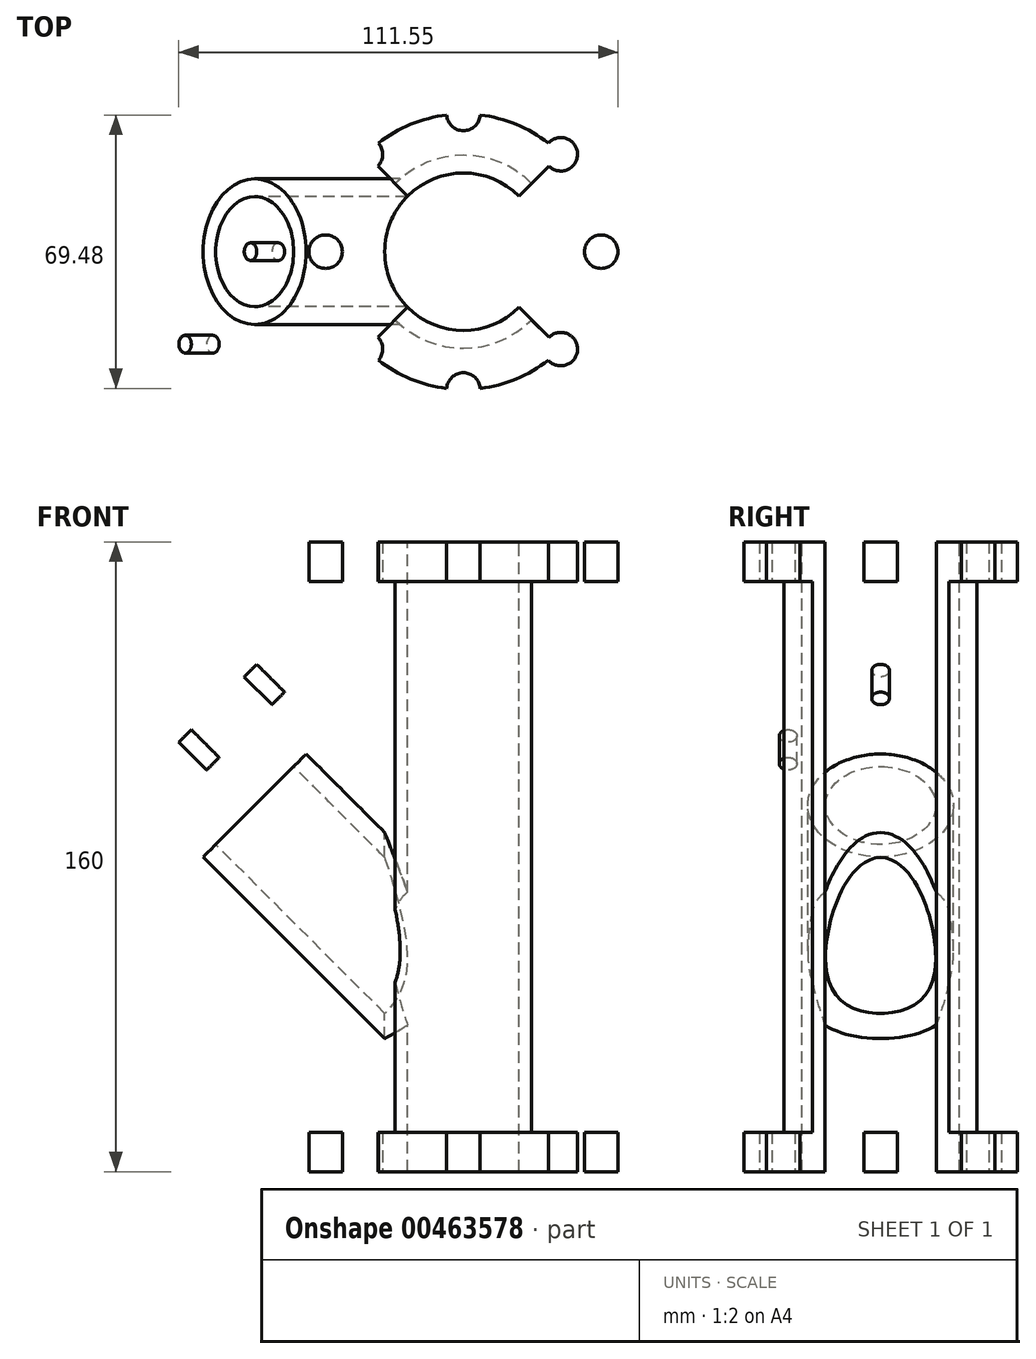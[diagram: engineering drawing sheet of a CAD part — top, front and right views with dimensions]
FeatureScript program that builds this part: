
annotation { "Feature Type Name" : "Feature", "Feature Type Description" : "" }
export const myFeature = defineFeature(function(context is Context, id is Id, definition is map)
    precondition{}
    {
        {
            var Q0;
            Q0=qCreatedBy(makeId("Top.planeOp"),FACE);
            var sketch = newSketch(context, id + "F0", { "sketchPlane" : qUnion([Q0])});
            skCircle(sketch, "E0", {"center": v(0, 0) * mm, "radius": 45 * mm});
            skSolve(sketch);
        }
        {
            var Q0;
            Q0 = qSketchRegion(id + "F0", true);
            extrude(context, id + "F1", {"entities" : qUnion([Q0]), "depth" : 10 * mm});
        }
        {
            var Q0;
            Q0=makeQuery(id+"F1.opExtrude","CAP_FACE",FACE,{"disambiguationData":[OSD([sQuery(id+"F0.wireOp",EDGE,"E0")])],"isStart":false});
            var sketch = newSketch(context, id + "F2", { "sketchPlane" : qUnion([Q0])});
            skCircle(sketch, "E1", {"center": v(0, 0) * mm, "radius": 24.5 * mm});
            skCircle(sketch, "E2", {"center": v(0, 0) * mm, "radius": 20 * mm});
            skSolve(sketch);
        }
        {
            var Q0;
            Q0 = qSketchRegion(id + "F2", true);
            var Q1;
            Q1=makeQuery(id+"F2.imprint","IMPRINT",FACE,{"disambiguationData":[TD([[makeQuery(id+"F2.imprint","IMPRINT",EDGE,{"derivedFrom":sQuery(id+"F2.wireOp",EDGE,"E2")}),1.0]])]});
            extrude(context, id + "F3", {"entities" : qUnion([Q0, Q1]), "operationType" : NewBodyOperationType.ADD, "depth" : 140 * mm});
        }
        {
            var Q0;
            Q0=makeQuery(id+"F3.opExtrude","CAP_FACE",FACE,{"disambiguationData":[OSD([sQuery(id+"F2.wireOp",EDGE,"E1")])],"isStart":false});
            var sketch = newSketch(context, id + "F4", { "sketchPlane" : qUnion([Q0])});
            skCircle(sketch, "E3", {"center": v(0, 0) * mm, "radius": 45 * mm});
            skCircle(sketch, "E4", {"center": v(0, 0) * mm, "radius": 24.5 * mm});
            skCircle(sketch, "E5", {"center": v(0, 0) * mm, "radius": 20 * mm});
            skSolve(sketch);
        }
        {
            var Q0;
            Q0 = qSketchRegion(id + "F4", true);
            var Q1;
            Q1=makeQuery(id+"F4.imprint","IMPRINT",FACE,{"disambiguationData":[TD([[makeQuery(id+"F4.imprint","IMPRINT",EDGE,{"derivedFrom":sQuery(id+"F4.wireOp",EDGE,"E5")}),1.0]])]});
            var Q2;
            Q2=makeQuery(id+"F4.imprint","IMPRINT",FACE,{"disambiguationData":[TD([[makeQuery(id+"F4.imprint","IMPRINT",EDGE,{"derivedFrom":sQuery(id+"F4.wireOp",EDGE,"E4")}),1.0]])]});
            extrude(context, id + "F5", {"entities" : qUnion([Q0, Q1, Q2]), "operationType" : NewBodyOperationType.ADD, "depth" : 10 * mm});
        }
        {
            var Q0;
            Q0=makeQuery(id+"F5.opExtrude","CAP_FACE",FACE,{"disambiguationData":[OSD([sQuery(id+"F4.wireOp",EDGE,"E3")])],"isStart":false});
            var sketch = newSketch(context, id + "F6", { "sketchPlane" : qUnion([Q0])});
            skSolve(sketch);
        }
        {
            var Q0;
            Q0=makeQuery(id+"F1.opExtrude","CAP_FACE",FACE,{"disambiguationData":[OSD([sQuery(id+"F0.wireOp",EDGE,"E0")])],"isStart":true});
            var sketch = newSketch(context, id + "F7", { "sketchPlane" : qUnion([Q0])});
            skCircle(sketch, "E6", {"center": v(0, 0) * mm, "radius": 35 * mm});
            skCircle(sketch, "E7", {"center": v(0, 35) * mm, "radius": 4.25 * mm});
            skCircle(sketch, "E8", {"center": v(35, 0) * mm, "radius": 4.25 * mm});
            skCircle(sketch, "E9", {"center": v(0, -35) * mm, "radius": 4.25 * mm});
            skCircle(sketch, "E10", {"center": v(-35, 0) * mm, "radius": 4.25 * mm});
            skLineSegment(sketch, "E11", {"start": v(0, 0) * mm, "end": v(7, 0) * mm});
            skLineSegment(sketch, "E12", {"start": v(0, 0) * mm, "end": v(0, -7) * mm});
            skLineSegment(sketch, "E13", {"start": v(0, 0) * mm, "end": v(-7, 0) * mm});
            skLineSegment(sketch, "E14", {"start": v(0, 0) * mm, "end": v(0, 7) * mm});
            skLineSegment(sketch, "E15", {"start": v(7, 0) * mm, "end": v(7, 7) * mm});
            skLineSegment(sketch, "E16", {"start": v(7, 7) * mm, "end": v(0, 7) * mm});
            skLineSegment(sketch, "E17", {"start": v(0, 7) * mm, "end": v(-7, 7) * mm});
            skLineSegment(sketch, "E18", {"start": v(-7, 7) * mm, "end": v(-7, 0) * mm});
            skLineSegment(sketch, "E19", {"start": v(-7, -7) * mm, "end": v(0, -7) * mm});
            skLineSegment(sketch, "E20", {"start": v(-7, -7) * mm, "end": v(-7, 0) * mm});
            skLineSegment(sketch, "E21", {"start": v(0, -7) * mm, "end": v(7, -7) * mm});
            skLineSegment(sketch, "E22", {"start": v(7, -7) * mm, "end": v(7, 0) * mm});
            skLineSegment(sketch, "E23", {"start": v(-7, -7) * mm, "end": v(7, 7) * mm});
            skLineSegment(sketch, "E24", {"start": v(7, -7) * mm, "end": v(-7, 7) * mm});
            skLineSegment(sketch, "E25", {"start": v(7, 7) * mm, "end": v(24.75, 24.75) * mm});
            skLineSegment(sketch, "E26", {"start": v(24.75, 24.75) * mm, "end": v(-24.75, -24.75) * mm});
            skLineSegment(sketch, "E27", {"start": v(-7, 7) * mm, "end": v(24.75, -24.75) * mm});
            skLineSegment(sketch, "E28", {"start": v(24.75, -24.75) * mm, "end": v(-24.75, 24.75) * mm});
            skCircle(sketch, "E29", {"center": v(-24.75, 24.75) * mm, "radius": 4.25 * mm});
            skCircle(sketch, "E30", {"center": v(24.75, 24.75) * mm, "radius": 4.25 * mm});
            skCircle(sketch, "E31", {"center": v(24.75, -24.75) * mm, "radius": 4.25 * mm});
            skCircle(sketch, "E32", {"center": v(-24.75, -24.75) * mm, "radius": 4.25 * mm});
            skSolve(sketch);
        }
        {
            var Q0;
            {var subQ0=sQuery(id+"F7.wireOp",EDGE,"E10");var subQ1=sQuery(id+"F7.wireOp",EDGE,"E6");var subQ2=makeQuery(id+"F7.imprint","INTERSECT",VERTEX,{"disambiguationData":[OD(0.0)],"derivedFrom":[subQ1,subQ0]});Q0=makeQuery(id+"F7.imprint","IMPRINT",FACE,{"disambiguationData":[TD([[makeQuery(id+"F7.imprint","IMPRINT",EDGE,{"disambiguationData":[TD([[subQ2,-1.0]])],"derivedFrom":subQ1}),-1.0]])]});}
            var Q1;
            {var subQ0=sQuery(id+"F7.wireOp",EDGE,"E10");var subQ1=sQuery(id+"F7.wireOp",EDGE,"E6");var subQ2=makeQuery(id+"F7.imprint","INTERSECT",VERTEX,{"disambiguationData":[OD(0.0)],"derivedFrom":[subQ1,subQ0]});Q1=makeQuery(id+"F7.imprint","IMPRINT",FACE,{"disambiguationData":[TD([[makeQuery(id+"F7.imprint","IMPRINT",EDGE,{"disambiguationData":[TD([[subQ2,-1.0]])],"derivedFrom":subQ1}),1.0]])]});}
            var Q2;
            {var subQ0=sQuery(id+"F7.wireOp",EDGE,"E9");var subQ1=sQuery(id+"F7.wireOp",EDGE,"E6");var subQ2=makeQuery(id+"F7.imprint","INTERSECT",VERTEX,{"disambiguationData":[OD(0.0)],"derivedFrom":[subQ1,subQ0]});Q2=makeQuery(id+"F7.imprint","IMPRINT",FACE,{"disambiguationData":[TD([[makeQuery(id+"F7.imprint","IMPRINT",EDGE,{"disambiguationData":[TD([[subQ2,-1.0]])],"derivedFrom":subQ1}),1.0]])]});}
            var Q3;
            {var subQ0=sQuery(id+"F7.wireOp",EDGE,"E9");var subQ1=sQuery(id+"F7.wireOp",EDGE,"E6");var subQ2=makeQuery(id+"F7.imprint","INTERSECT",VERTEX,{"disambiguationData":[OD(0.0)],"derivedFrom":[subQ1,subQ0]});Q3=makeQuery(id+"F7.imprint","IMPRINT",FACE,{"disambiguationData":[TD([[makeQuery(id+"F7.imprint","IMPRINT",EDGE,{"disambiguationData":[TD([[subQ2,-1.0]])],"derivedFrom":subQ1}),-1.0]])]});}
            var Q4;
            {var subQ0=sQuery(id+"F7.wireOp",EDGE,"E8");var subQ1=sQuery(id+"F7.wireOp",EDGE,"E6");var subQ2=makeQuery(id+"F7.imprint","INTERSECT",VERTEX,{"disambiguationData":[OD(0.0)],"derivedFrom":[subQ1,subQ0]});Q4=makeQuery(id+"F7.imprint","IMPRINT",FACE,{"disambiguationData":[TD([[makeQuery(id+"F7.imprint","IMPRINT",EDGE,{"disambiguationData":[TD([[subQ2,1.0]])],"derivedFrom":subQ1}),1.0]])]});}
            var Q5;
            {var subQ0=sQuery(id+"F7.wireOp",EDGE,"E8");var subQ1=sQuery(id+"F7.wireOp",EDGE,"E6");var subQ2=makeQuery(id+"F7.imprint","INTERSECT",VERTEX,{"disambiguationData":[OD(0.0)],"derivedFrom":[subQ1,subQ0]});Q5=makeQuery(id+"F7.imprint","IMPRINT",FACE,{"disambiguationData":[TD([[makeQuery(id+"F7.imprint","IMPRINT",EDGE,{"disambiguationData":[TD([[subQ2,1.0]])],"derivedFrom":subQ1}),-1.0]])]});}
            var Q6;
            {var subQ0=sQuery(id+"F7.wireOp",EDGE,"E6");var subQ1=makeQuery(id+"F7.imprint","INTERSECT",VERTEX,{"disambiguationData":[OD(0.0)],"derivedFrom":[subQ0,sQuery(id+"F7.wireOp",EDGE,"E26")]});Q6=makeQuery(id+"F7.imprint","IMPRINT",FACE,{"disambiguationData":[TD([[makeQuery(id+"F7.imprint","IMPRINT",EDGE,{"disambiguationData":[TD([[subQ1,1.0]])],"derivedFrom":subQ0}),-1.0]])]});}
            var Q7;
            {var subQ0=sQuery(id+"F7.wireOp",EDGE,"E26");var subQ1=sQuery(id+"F7.wireOp",EDGE,"E6");var subQ2=makeQuery(id+"F7.imprint","INTERSECT",VERTEX,{"disambiguationData":[OD(0.0)],"derivedFrom":[subQ1,subQ0]});Q7=makeQuery(id+"F7.imprint","IMPRINT",FACE,{"disambiguationData":[TD([[makeQuery(id+"F7.imprint","IMPRINT",EDGE,{"disambiguationData":[TD([[subQ2,1.0]])],"derivedFrom":subQ1}),1.0]])]});}
            var Q8;
            {var subQ0=sQuery(id+"F7.wireOp",EDGE,"E26");var subQ1=sQuery(id+"F7.wireOp",EDGE,"E6");var subQ2=makeQuery(id+"F7.imprint","INTERSECT",VERTEX,{"disambiguationData":[OD(0.0)],"derivedFrom":[subQ1,subQ0]});Q8=makeQuery(id+"F7.imprint","IMPRINT",FACE,{"disambiguationData":[TD([[makeQuery(id+"F7.imprint","IMPRINT",EDGE,{"disambiguationData":[TD([[subQ2,-1.0]])],"derivedFrom":subQ1}),1.0]])]});}
            var Q9;
            {var subQ0=sQuery(id+"F7.wireOp",EDGE,"E6");var subQ1=makeQuery(id+"F7.imprint","INTERSECT",VERTEX,{"disambiguationData":[OD(1.0)],"derivedFrom":[subQ0,sQuery(id+"F7.wireOp",EDGE,"E28")]});Q9=makeQuery(id+"F7.imprint","IMPRINT",FACE,{"disambiguationData":[TD([[makeQuery(id+"F7.imprint","IMPRINT",EDGE,{"disambiguationData":[TD([[subQ1,1.0]])],"derivedFrom":subQ0}),-1.0]])]});}
            var Q10;
            {var subQ0=sQuery(id+"F7.wireOp",EDGE,"E28");var subQ1=sQuery(id+"F7.wireOp",EDGE,"E6");var subQ2=makeQuery(id+"F7.imprint","INTERSECT",VERTEX,{"disambiguationData":[OD(1.0)],"derivedFrom":[subQ1,subQ0]});Q10=makeQuery(id+"F7.imprint","IMPRINT",FACE,{"disambiguationData":[TD([[makeQuery(id+"F7.imprint","IMPRINT",EDGE,{"disambiguationData":[TD([[subQ2,1.0]])],"derivedFrom":subQ1}),1.0]])]});}
            var Q11;
            {var subQ0=sQuery(id+"F7.wireOp",EDGE,"E28");var subQ1=sQuery(id+"F7.wireOp",EDGE,"E6");var subQ2=makeQuery(id+"F7.imprint","INTERSECT",VERTEX,{"disambiguationData":[OD(1.0)],"derivedFrom":[subQ1,subQ0]});Q11=makeQuery(id+"F7.imprint","IMPRINT",FACE,{"disambiguationData":[TD([[makeQuery(id+"F7.imprint","IMPRINT",EDGE,{"disambiguationData":[TD([[subQ2,-1.0]])],"derivedFrom":subQ1}),1.0]])]});}
            var Q12;
            {var subQ0=sQuery(id+"F7.wireOp",EDGE,"E6");var subQ1=makeQuery(id+"F7.imprint","INTERSECT",VERTEX,{"disambiguationData":[OD(1.0)],"derivedFrom":[subQ0,sQuery(id+"F7.wireOp",EDGE,"E26")]});Q12=makeQuery(id+"F7.imprint","IMPRINT",FACE,{"disambiguationData":[TD([[makeQuery(id+"F7.imprint","IMPRINT",EDGE,{"disambiguationData":[TD([[subQ1,1.0]])],"derivedFrom":subQ0}),-1.0]])]});}
            var Q13;
            {var subQ0=sQuery(id+"F7.wireOp",EDGE,"E26");var subQ1=sQuery(id+"F7.wireOp",EDGE,"E6");var subQ2=makeQuery(id+"F7.imprint","INTERSECT",VERTEX,{"disambiguationData":[OD(1.0)],"derivedFrom":[subQ1,subQ0]});Q13=makeQuery(id+"F7.imprint","IMPRINT",FACE,{"disambiguationData":[TD([[makeQuery(id+"F7.imprint","IMPRINT",EDGE,{"disambiguationData":[TD([[subQ2,1.0]])],"derivedFrom":subQ1}),1.0]])]});}
            var Q14;
            {var subQ0=sQuery(id+"F7.wireOp",EDGE,"E26");var subQ1=sQuery(id+"F7.wireOp",EDGE,"E6");var subQ2=makeQuery(id+"F7.imprint","INTERSECT",VERTEX,{"disambiguationData":[OD(1.0)],"derivedFrom":[subQ1,subQ0]});Q14=makeQuery(id+"F7.imprint","IMPRINT",FACE,{"disambiguationData":[TD([[makeQuery(id+"F7.imprint","IMPRINT",EDGE,{"disambiguationData":[TD([[subQ2,-1.0]])],"derivedFrom":subQ1}),1.0]])]});}
            var Q15;
            {var subQ0=sQuery(id+"F7.wireOp",EDGE,"E6");var subQ1=makeQuery(id+"F7.imprint","INTERSECT",VERTEX,{"disambiguationData":[OD(0.0)],"derivedFrom":[subQ0,sQuery(id+"F7.wireOp",EDGE,"E28")]});Q15=makeQuery(id+"F7.imprint","IMPRINT",FACE,{"disambiguationData":[TD([[makeQuery(id+"F7.imprint","IMPRINT",EDGE,{"disambiguationData":[TD([[subQ1,1.0]])],"derivedFrom":subQ0}),-1.0]])]});}
            var Q16;
            {var subQ0=sQuery(id+"F7.wireOp",EDGE,"E28");var subQ1=sQuery(id+"F7.wireOp",EDGE,"E6");var subQ2=makeQuery(id+"F7.imprint","INTERSECT",VERTEX,{"disambiguationData":[OD(0.0)],"derivedFrom":[subQ1,subQ0]});Q16=makeQuery(id+"F7.imprint","IMPRINT",FACE,{"disambiguationData":[TD([[makeQuery(id+"F7.imprint","IMPRINT",EDGE,{"disambiguationData":[TD([[subQ2,1.0]])],"derivedFrom":subQ1}),1.0]])]});}
            var Q17;
            {var subQ0=sQuery(id+"F7.wireOp",EDGE,"E28");var subQ1=sQuery(id+"F7.wireOp",EDGE,"E6");var subQ2=makeQuery(id+"F7.imprint","INTERSECT",VERTEX,{"disambiguationData":[OD(0.0)],"derivedFrom":[subQ1,subQ0]});Q17=makeQuery(id+"F7.imprint","IMPRINT",FACE,{"disambiguationData":[TD([[makeQuery(id+"F7.imprint","IMPRINT",EDGE,{"disambiguationData":[TD([[subQ2,-1.0]])],"derivedFrom":subQ1}),1.0]])]});}
            var Q18;
            {var subQ0=sQuery(id+"F7.wireOp",EDGE,"E7");var subQ1=sQuery(id+"F7.wireOp",EDGE,"E6");var subQ2=makeQuery(id+"F7.imprint","INTERSECT",VERTEX,{"disambiguationData":[OD(0.0)],"derivedFrom":[subQ1,subQ0]});Q18=makeQuery(id+"F7.imprint","IMPRINT",FACE,{"disambiguationData":[TD([[makeQuery(id+"F7.imprint","IMPRINT",EDGE,{"disambiguationData":[TD([[subQ2,-1.0]])],"derivedFrom":subQ1}),1.0]])]});}
            var Q19;
            {var subQ0=sQuery(id+"F7.wireOp",EDGE,"E7");var subQ1=sQuery(id+"F7.wireOp",EDGE,"E6");var subQ2=makeQuery(id+"F7.imprint","INTERSECT",VERTEX,{"disambiguationData":[OD(0.0)],"derivedFrom":[subQ1,subQ0]});Q19=makeQuery(id+"F7.imprint","IMPRINT",FACE,{"disambiguationData":[TD([[makeQuery(id+"F7.imprint","IMPRINT",EDGE,{"disambiguationData":[TD([[subQ2,-1.0]])],"derivedFrom":subQ1}),-1.0]])]});}
            extrude(context, id + "F8", {"entities" : qUnion([Q0, Q1, Q2, Q3, Q4, Q5, Q6, Q7, Q8, Q9, Q10, Q11, Q12, Q13, Q14, Q15, Q16, Q17, Q18, Q19]), "operationType" : NewBodyOperationType.REMOVE, "oppositeDirection" : true, "depth" : 195 * mm});
        }
        {
            var Q0;
            Q0=qCreatedBy(makeId("Front.planeOp"),FACE);
            var sketch = newSketch(context, id + "F9", { "sketchPlane" : qUnion([Q0])});
            skLineSegment(sketch, "E33", {"start": v(0, 0) * mm, "end": v(0, 40) * mm});
            skLineSegment(sketch, "E34", {"start": v(0, 40) * mm, "end": v(0, 93.3) * mm});
            skLineSegment(sketch, "E35", {"start": v(0, 40) * mm, "end": v(-63.64, 103.64) * mm});
            skLineSegment(sketch, "E36", {"start": v(-63.64, 103.64) * mm, "end": v(-50.56, 116.72) * mm});
            skLineSegment(sketch, "E37", {"start": v(-50.56, 116.72) * mm, "end": v(-76.72, 90.56) * mm});
            skLineSegment(sketch, "E38", {"start": v(-76.72, 90.56) * mm, "end": v(0, 13.84) * mm});
            skLineSegment(sketch, "E39", {"start": v(0, 13.84) * mm, "end": v(0, 40) * mm});
            skLineSegment(sketch, "E40", {"start": v(-50.56, 116.72) * mm, "end": v(6.24, 59.92) * mm});
            skLineSegment(sketch, "E41", {"start": v(6.24, 59.92) * mm, "end": v(0, 13.84) * mm});
            skSolve(sketch);
        }
        {
            var Q0;
            Q0 = qSketchRegion(id + "F9", true);
            extrude(context, id + "F10", {"entities" : qUnion([Q0]), "operationType" : NewBodyOperationType.ADD, "endBound" : BoundingType.SYMMETRIC, "depth" : 37 * mm});
        }
        {
            var Q0;
            Q0=makeQuery(id+"F10.opExtrude","CAP_EDGE",EDGE,{"disambiguationData":[OSD([sQuery(id+"F9.wireOp",EDGE,"E38")])],"isStart":true});
            var Q1;
            Q1=makeQuery(id+"F10.opExtrude","CAP_EDGE",EDGE,{"disambiguationData":[OSD([sQuery(id+"F9.wireOp",EDGE,"E38")])],"isStart":false});
            var Q2;
            Q2=makeQuery(id+"F10.opExtrude","CAP_EDGE",EDGE,{"disambiguationData":[OSD([sQuery(id+"F9.wireOp",EDGE,"E40")])],"isStart":false});
            var Q3;
            Q3=makeQuery(id+"F10.opExtrude","CAP_EDGE",EDGE,{"disambiguationData":[OSD([sQuery(id+"F9.wireOp",EDGE,"E40")])],"isStart":true});
            fillet(context, id + "F11", {"entities" : qUnion([Q0, Q1, Q2, Q3]), "radius" : 18.5 * mm, "tangentPropagation" : true, "allowEdgeOverflow" : false});
        }
        {
            var Q0;
            Q0=makeQuery(id+"F10.opExtrude","SWEPT_FACE",FACE,{"disambiguationData":[OSD([sQuery(id+"F9.wireOp",EDGE,"E37")])]});
            var sketch = newSketch(context, id + "F12", { "sketchPlane" : qUnion([Q0])});
            skCircle(sketch, "E42", {"center": v(0, 28.28) * mm, "radius": 28.5 * mm});
            skSolve(sketch);
        }
        {
            var Q0;
            Q0 = qSketchRegion(id + "F12", true);
            extrude(context, id + "F13", {"entities" : qUnion([Q0]), "operationType" : NewBodyOperationType.ADD, "depth" : 10 * mm});
        }
        {
            var Q0;
            Q0=makeQuery(id+"F13.opExtrude","CAP_FACE",FACE,{"disambiguationData":[OSD([sQuery(id+"F12.wireOp",EDGE,"E42")])],"isStart":false});
            var sketch = newSketch(context, id + "F14", { "sketchPlane" : qUnion([Q0])});
            skCircle(sketch, "E43", {"center": v(0, 28.28) * mm, "radius": 23.5 * mm});
            skCircle(sketch, "E44", {"center": v(0, 51.78) * mm, "radius": 2.25 * mm});
            skCircle(sketch, "E45", {"center": v(23.5, 28.28) * mm, "radius": 2.25 * mm});
            skCircle(sketch, "E46", {"center": v(-23.5, 28.28) * mm, "radius": 2.25 * mm});
            skCircle(sketch, "E47", {"center": v(0, 4.78) * mm, "radius": 2.25 * mm});
            skSolve(sketch);
        }
        {
            var Q0;
            {var subQ0=sQuery(id+"F14.wireOp",EDGE,"E44");var subQ1=sQuery(id+"F14.wireOp",EDGE,"E43");var subQ2=makeQuery(id+"F14.imprint","INTERSECT",VERTEX,{"disambiguationData":[OD(0.0)],"derivedFrom":[subQ1,subQ0]});Q0=makeQuery(id+"F14.imprint","IMPRINT",FACE,{"disambiguationData":[TD([[makeQuery(id+"F14.imprint","IMPRINT",EDGE,{"disambiguationData":[TD([[subQ2,-1.0]])],"derivedFrom":subQ1}),1.0]])]});}
            var Q1;
            {var subQ0=sQuery(id+"F14.wireOp",EDGE,"E44");var subQ1=sQuery(id+"F14.wireOp",EDGE,"E43");var subQ2=makeQuery(id+"F14.imprint","INTERSECT",VERTEX,{"disambiguationData":[OD(0.0)],"derivedFrom":[subQ1,subQ0]});Q1=makeQuery(id+"F14.imprint","IMPRINT",FACE,{"disambiguationData":[TD([[makeQuery(id+"F14.imprint","IMPRINT",EDGE,{"disambiguationData":[TD([[subQ2,-1.0]])],"derivedFrom":subQ1}),-1.0]])]});}
            var Q2;
            {var subQ0=sQuery(id+"F14.wireOp",EDGE,"E46");var subQ1=sQuery(id+"F14.wireOp",EDGE,"E43");var subQ2=makeQuery(id+"F14.imprint","INTERSECT",VERTEX,{"disambiguationData":[OD(0.0)],"derivedFrom":[subQ1,subQ0]});Q2=makeQuery(id+"F14.imprint","IMPRINT",FACE,{"disambiguationData":[TD([[makeQuery(id+"F14.imprint","IMPRINT",EDGE,{"disambiguationData":[TD([[subQ2,-1.0]])],"derivedFrom":subQ1}),-1.0]])]});}
            var Q3;
            {var subQ0=sQuery(id+"F14.wireOp",EDGE,"E46");var subQ1=sQuery(id+"F14.wireOp",EDGE,"E43");var subQ2=makeQuery(id+"F14.imprint","INTERSECT",VERTEX,{"disambiguationData":[OD(0.0)],"derivedFrom":[subQ1,subQ0]});Q3=makeQuery(id+"F14.imprint","IMPRINT",FACE,{"disambiguationData":[TD([[makeQuery(id+"F14.imprint","IMPRINT",EDGE,{"disambiguationData":[TD([[subQ2,-1.0]])],"derivedFrom":subQ1}),1.0]])]});}
            var Q4;
            {var subQ0=sQuery(id+"F14.wireOp",EDGE,"E47");var subQ1=sQuery(id+"F14.wireOp",EDGE,"E43");var subQ2=makeQuery(id+"F14.imprint","INTERSECT",VERTEX,{"disambiguationData":[OD(0.0)],"derivedFrom":[subQ1,subQ0]});Q4=makeQuery(id+"F14.imprint","IMPRINT",FACE,{"disambiguationData":[TD([[makeQuery(id+"F14.imprint","IMPRINT",EDGE,{"disambiguationData":[TD([[subQ2,-1.0]])],"derivedFrom":subQ1}),1.0]])]});}
            var Q5;
            {var subQ0=sQuery(id+"F14.wireOp",EDGE,"E47");var subQ1=sQuery(id+"F14.wireOp",EDGE,"E43");var subQ2=makeQuery(id+"F14.imprint","INTERSECT",VERTEX,{"disambiguationData":[OD(0.0)],"derivedFrom":[subQ1,subQ0]});Q5=makeQuery(id+"F14.imprint","IMPRINT",FACE,{"disambiguationData":[TD([[makeQuery(id+"F14.imprint","IMPRINT",EDGE,{"disambiguationData":[TD([[subQ2,-1.0]])],"derivedFrom":subQ1}),-1.0]])]});}
            var Q6;
            {var subQ0=sQuery(id+"F14.wireOp",EDGE,"E45");var subQ1=sQuery(id+"F14.wireOp",EDGE,"E43");var subQ2=makeQuery(id+"F14.imprint","INTERSECT",VERTEX,{"disambiguationData":[OD(0.0)],"derivedFrom":[subQ1,subQ0]});Q6=makeQuery(id+"F14.imprint","IMPRINT",FACE,{"disambiguationData":[TD([[makeQuery(id+"F14.imprint","IMPRINT",EDGE,{"disambiguationData":[TD([[subQ2,1.0]])],"derivedFrom":subQ1}),1.0]])]});}
            var Q7;
            {var subQ0=sQuery(id+"F14.wireOp",EDGE,"E45");var subQ1=sQuery(id+"F14.wireOp",EDGE,"E43");var subQ2=makeQuery(id+"F14.imprint","INTERSECT",VERTEX,{"disambiguationData":[OD(0.0)],"derivedFrom":[subQ1,subQ0]});Q7=makeQuery(id+"F14.imprint","IMPRINT",FACE,{"disambiguationData":[TD([[makeQuery(id+"F14.imprint","IMPRINT",EDGE,{"disambiguationData":[TD([[subQ2,1.0]])],"derivedFrom":subQ1}),-1.0]])]});}
            extrude(context, id + "F15", {"entities" : qUnion([Q0, Q1, Q2, Q3, Q4, Q5, Q6, Q7]), "operationType" : NewBodyOperationType.REMOVE, "oppositeDirection" : true, "depth" : 25 * mm});
        }
        {
            var Q0;
            Q0=makeQuery(id+"F13.opExtrude","CAP_FACE",FACE,{"disambiguationData":[OSD([sQuery(id+"F12.wireOp",EDGE,"E42")])],"isStart":false});
            var sketch = newSketch(context, id + "F16", { "sketchPlane" : qUnion([Q0])});
            skCircle(sketch, "E48", {"center": v(0, 28.28) * mm, "radius": 14 * mm});
            skSolve(sketch);
        }
        {
            var Q0;
            Q0 = qSketchRegion(id + "F16", true);
            extrude(context, id + "F17", {"entities" : qUnion([Q0]), "operationType" : NewBodyOperationType.REMOVE, "oppositeDirection" : true, "depth" : 99.7 * mm});
        }
        {
            var Q0;
            Q0=makeQuery(id+"F6.imprint","IMPRINT",FACE,{"disambiguationData":[TD([[makeQuery(id+"F6.imprint","IMPRINT",EDGE,{"derivedFrom":makeQuery(id+"F5.opExtrude","CAP_EDGE",EDGE,{"disambiguationData":[OSD([sQuery(id+"F4.wireOp",EDGE,"E3")])],"isStart":false})}),1.0]])]});
            var sketch = newSketch(context, id + "F18", { "sketchPlane" : qUnion([Q0])});
            skCircle(sketch, "E49", {"center": v(0, 0) * mm, "radius": 20 * mm});
            skSolve(sketch);
        }
        {
            var Q0;
            Q0 = qSketchRegion(id + "F18", true);
            extrude(context, id + "F19", {"entities" : qUnion([Q0]), "operationType" : NewBodyOperationType.REMOVE, "oppositeDirection" : true, "depth" : 202.6 * mm});
        }
    });
